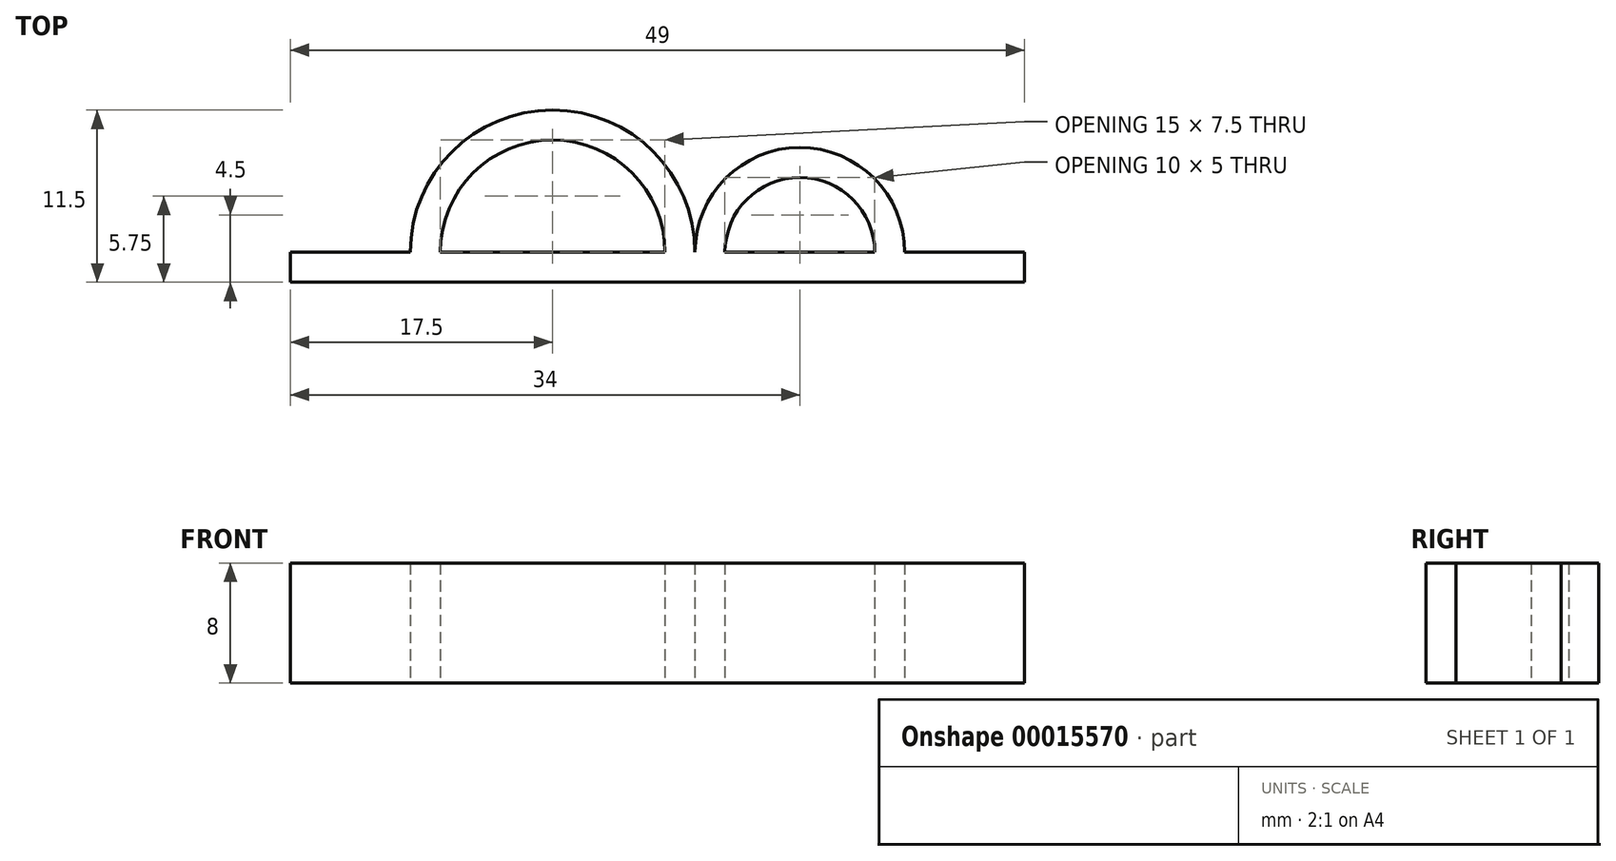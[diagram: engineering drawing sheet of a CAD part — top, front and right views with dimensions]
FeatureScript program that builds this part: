
annotation { "Feature Type Name" : "Feature", "Feature Type Description" : "" }
export const myFeature = defineFeature(function(context is Context, id is Id, definition is map)
    precondition{}
    {
        {
            var Q0;
            Q0=qCreatedBy(makeId("Top.planeOp"),FACE);
            var sketch = newSketch(context, id + "F0", { "sketchPlane" : qUnion([Q0])});
            skArc(sketch, "E0", {"start": v(9.5, 0) * mm, "mid": v(0, 9.5) * mm, "end": v(-9.5, 0) * mm});
            skArc(sketch, "E1", {"start": v(7.5, 0) * mm, "mid": v(0, 7.5) * mm, "end": v(-7.5, 0) * mm});
            skArc(sketch, "E2", {"start": v(23.5, 0) * mm, "mid": v(16.5, 7) * mm, "end": v(9.5, 0) * mm});
            skArc(sketch, "E3", {"start": v(21.5, 0) * mm, "mid": v(16.5, 5) * mm, "end": v(11.5, 0) * mm});
            skLineSegment(sketch, "E4", {"start": v(-9.5, 0) * mm, "end": v(23.5, 0) * mm});
            skLineSegment(sketch, "E5", {"start": v(23.5, 0) * mm, "end": v(31.5, 0) * mm});
            skLineSegment(sketch, "E6", {"start": v(31.5, 0) * mm, "end": v(31.5, -2) * mm});
            skLineSegment(sketch, "E7", {"start": v(-9.5, 0) * mm, "end": v(-17.5, 0) * mm});
            skLineSegment(sketch, "E8", {"start": v(-17.5, 0) * mm, "end": v(-17.5, -2) * mm});
            skLineSegment(sketch, "E9", {"start": v(-17.5, -2) * mm, "end": v(31.5, -2) * mm});
            skSolve(sketch);
        }
        {
            var Q0;
            Q0=qSketchRegion(id+"F0",true);
            extrude(context, id + "F1", {"entities" : qUnion([Q0]), "depth" : 8 * mm});
        }
    });
